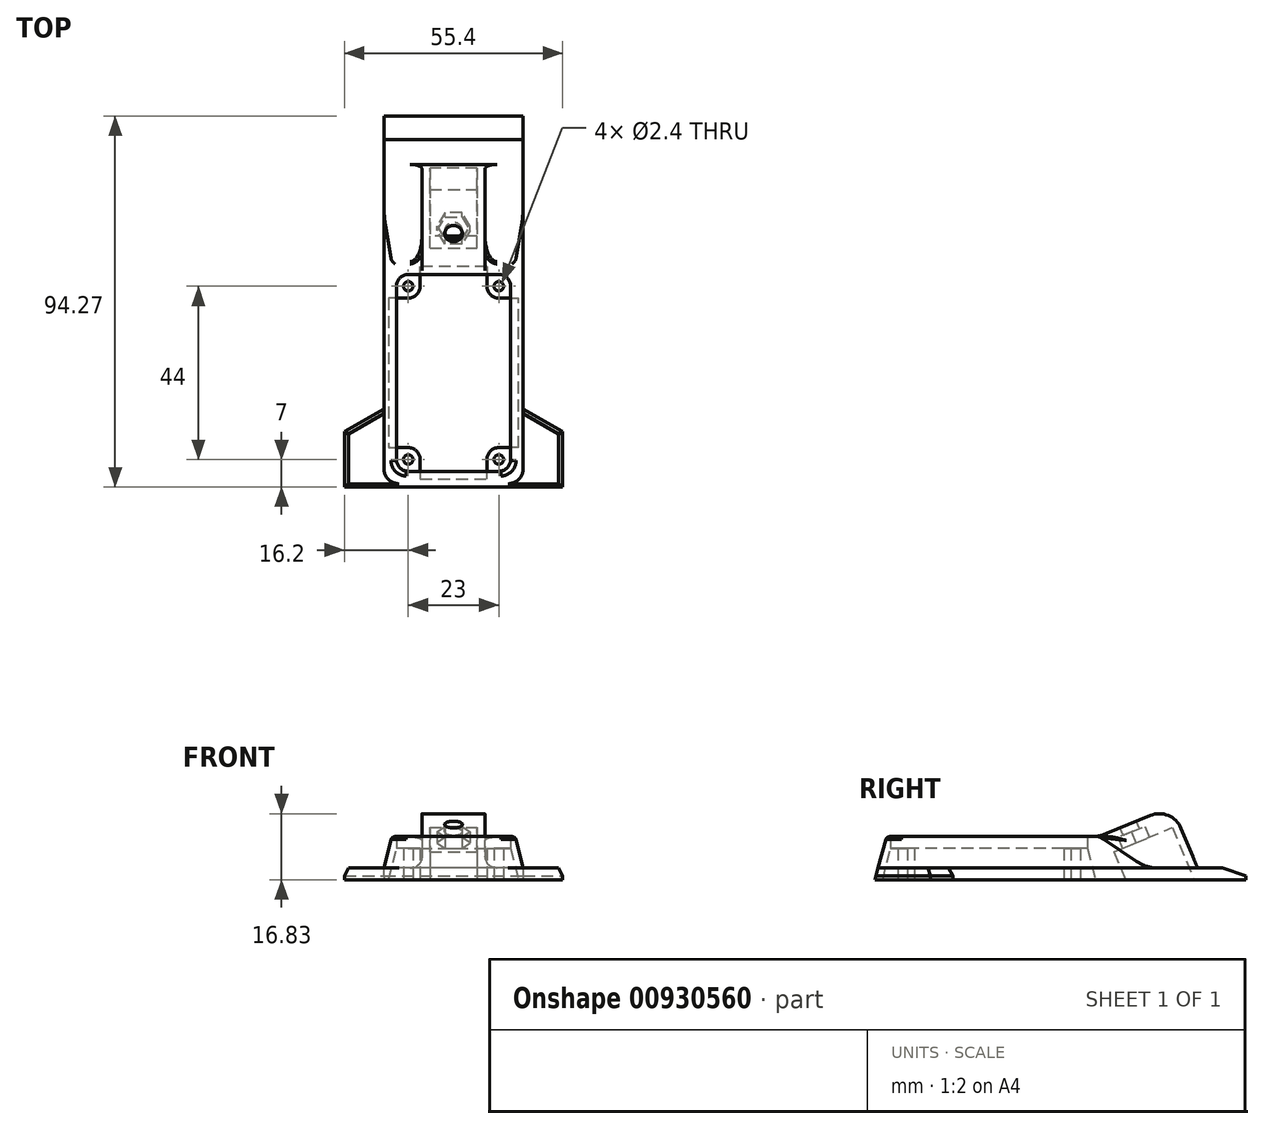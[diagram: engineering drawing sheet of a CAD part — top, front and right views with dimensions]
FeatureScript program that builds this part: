
annotation { "Feature Type Name" : "Feature", "Feature Type Description" : "" }
export const myFeature = defineFeature(function(context is Context, id is Id, definition is map)
    precondition{}
    {
        {
            var Q0;
            Q0=qCreatedBy(makeId("Top.planeOp"),FACE);
            var sketch = newSketch(context, id + "F0", { "sketchPlane" : qUnion([Q0])});
            skLineSegment(sketch, "E0", {"start": v(-28, 0) * mm, "end": v(28, 0) * mm, "construction": true});
            skLineSegment(sketch, "E1", {"start": v(28, 0) * mm, "end": v(28, 14.23) * mm, "construction": true});
            skLineSegment(sketch, "E2", {"start": v(28, 14.23) * mm, "end": v(18, 20) * mm, "construction": true});
            skLineSegment(sketch, "E3", {"start": v(18, 20) * mm, "end": v(18, 100.26) * mm, "construction": true});
            skLineSegment(sketch, "E4", {"start": v(18, 100.26) * mm, "end": v(-18, 100.26) * mm, "construction": true});
            skLineSegment(sketch, "E5", {"start": v(-18, 100.26) * mm, "end": v(-18, 20) * mm, "construction": true});
            skLineSegment(sketch, "E6", {"start": v(-18, 20) * mm, "end": v(-28, 14.23) * mm, "construction": true});
            skLineSegment(sketch, "E7", {"start": v(-28, 14.23) * mm, "end": v(-28, 0) * mm, "construction": true});
            skLineSegment(sketch, "E8", {"start": v(-18, 94.27) * mm, "end": v(18, 94.27) * mm, "construction": true});
            skLineSegment(sketch, "E9.bottom", {"start": v(-10.5, 55) * mm, "end": v(10.5, 55) * mm, "construction": true});
            skLineSegment(sketch, "E9.top", {"start": v(-10.5, 3) * mm, "end": v(10.5, 3) * mm, "construction": true});
            skLineSegment(sketch, "E9.left", {"start": v(-15.5, 50) * mm, "end": v(-15.5, 8) * mm, "construction": true});
            skLineSegment(sketch, "E9.right", {"start": v(15.5, 50) * mm, "end": v(15.5, 8) * mm, "construction": true});
            skLineSegment(sketch, "E10", {"start": v(-17.7, 19.83) * mm, "end": v(-17.7, 94.27) * mm});
            skLineSegment(sketch, "E11", {"start": v(-17.7, 94.27) * mm, "end": v(17.7, 94.27) * mm});
            skLineSegment(sketch, "E12", {"start": v(17.7, 94.27) * mm, "end": v(17.7, 19.83) * mm});
            skLineSegment(sketch, "E13", {"start": v(-17.7, 19.83) * mm, "end": v(-27.7, 14.05) * mm});
            skLineSegment(sketch, "E14", {"start": v(-27.7, 14.05) * mm, "end": v(-27.7, 0) * mm});
            skLineSegment(sketch, "E15", {"start": v(-27.7, 0) * mm, "end": v(27.7, 0) * mm});
            skLineSegment(sketch, "E16", {"start": v(27.7, 0) * mm, "end": v(27.7, 14.05) * mm});
            skLineSegment(sketch, "E17", {"start": v(27.7, 14.05) * mm, "end": v(17.7, 19.83) * mm});
            skCircle(sketch, "E18", {"center": v(-11.5, 51) * mm, "radius": 1.2 * mm});
            skCircle(sketch, "E19", {"center": v(11.5, 51) * mm, "radius": 1.2 * mm});
            skCircle(sketch, "E20", {"center": v(-11.5, 7) * mm, "radius": 1.2 * mm});
            skCircle(sketch, "E21", {"center": v(11.5, 7) * mm, "radius": 1.2 * mm});
            skArc(sketch, "E22", {"start": v(-11.5, 48) * mm, "mid": v(-9.38, 48.88) * mm, "end": v(-8.5, 51) * mm});
            skArc(sketch, "E23", {"start": v(8.5, 51) * mm, "mid": v(9.38, 48.88) * mm, "end": v(11.5, 48) * mm});
            skArc(sketch, "E24", {"start": v(-8.5, 7) * mm, "mid": v(-9.38, 9.12) * mm, "end": v(-11.5, 10) * mm});
            skArc(sketch, "E25", {"start": v(11.5, 10) * mm, "mid": v(9.38, 9.12) * mm, "end": v(8.5, 7) * mm});
            skLineSegment(sketch, "E26", {"start": v(-11.5, 48) * mm, "end": v(-14.5, 48) * mm});
            skLineSegment(sketch, "E27", {"start": v(-14.5, 48) * mm, "end": v(-14.5, 10) * mm});
            skLineSegment(sketch, "E28", {"start": v(-8.5, 54) * mm, "end": v(8.5, 54) * mm});
            skLineSegment(sketch, "E29", {"start": v(-8.5, 54) * mm, "end": v(-8.5, 51) * mm});
            skPoint(sketch, "E30.visualSharp", {"position": v(-15.5, 55) * mm});
            skArc(sketch, "E30.filletArc", {"start": v(-10.5, 55) * mm, "mid": v(-14.04, 53.54) * mm, "end": v(-15.5, 50) * mm, "construction": true});
            skPoint(sketch, "E31.visualSharp", {"position": v(15.5, 55) * mm});
            skArc(sketch, "E31.filletArc", {"start": v(15.5, 50) * mm, "mid": v(14.04, 53.54) * mm, "end": v(10.5, 55) * mm, "construction": true});
            skPoint(sketch, "E32.visualSharp", {"position": v(-15.5, 3) * mm});
            skArc(sketch, "E32.filletArc", {"start": v(-15.5, 8) * mm, "mid": v(-14.04, 4.46) * mm, "end": v(-10.5, 3) * mm, "construction": true});
            skPoint(sketch, "E33.visualSharp", {"position": v(15.5, 3) * mm});
            skArc(sketch, "E33.filletArc", {"start": v(10.5, 3) * mm, "mid": v(14.04, 4.46) * mm, "end": v(15.5, 8) * mm, "construction": true});
            skLineSegment(sketch, "E34", {"start": v(8.5, 54) * mm, "end": v(8.5, 51) * mm});
            skLineSegment(sketch, "E35", {"start": v(11.5, 48) * mm, "end": v(14.5, 48) * mm});
            skLineSegment(sketch, "E36", {"start": v(14.5, 48) * mm, "end": v(14.5, 10) * mm});
            skLineSegment(sketch, "E37", {"start": v(14.5, 10) * mm, "end": v(11.5, 10) * mm});
            skLineSegment(sketch, "E38", {"start": v(-11.5, 10) * mm, "end": v(-14.5, 10) * mm});
            skLineSegment(sketch, "E39", {"start": v(-8.5, 7) * mm, "end": v(-8.5, 4) * mm});
            skLineSegment(sketch, "E40", {"start": v(-8.5, 4) * mm, "end": v(8.5, 4) * mm});
            skLineSegment(sketch, "E41", {"start": v(8.5, 4) * mm, "end": v(8.5, 7) * mm});
            skSolve(sketch);
        }
        {
            var Q0;
            Q0=qSketchRegion(id+"F0",true);
            extrude(context, id + "F1", {"entities" : qUnion([Q0]), "depth" : 3 * mm, "offsetDistance" : 25 * mm});
        }
        {
            var Q0;
            Q0=makeQuery(id+"F1.opExtrude","SWEPT_FACE",FACE,{"disambiguationData":[OSD([sQuery(id+"F0.wireOp",EDGE,"E14")])]});
            var sketch = newSketch(context, id + "F2", { "sketchPlane" : qUnion([Q0])});
            skLineSegment(sketch, "E42", {"start": v(0, 0) * mm, "end": v(0, 3) * mm});
            skLineSegment(sketch, "E43", {"start": v(0, 3) * mm, "end": v(1.25, 3) * mm});
            skLineSegment(sketch, "E44", {"start": v(1.25, 3) * mm, "end": v(0, 0) * mm});
            skSolve(sketch);
        }
        {
            var Q0;
            Q0=qSketchRegion(id+"F2",true);
            var Q1;
            Q1=makeQuery(id+"F1.opExtrude","SWEPT_FACE",FACE,{"disambiguationData":[OSD([sQuery(id+"F0.wireOp",EDGE,"E16")])]});
            extrude(context, id + "F3", {"entities" : qUnion([Q0]), "operationType" : NewBodyOperationType.ADD, "endBound" : BoundingType.UP_TO_SURFACE, "oppositeDirection" : true, "depth" : 25 * mm, "endBoundEntityFace" : qUnion([Q1]), "offsetDistance" : 25 * mm});
        }
        {
            var Q0;
            Q0=makeQuery(id+"F3.boolean.opBoolean","MERGE",FACE,{"derivedFrom":[makeQuery(id+"F1.opExtrude","CAP_FACE",FACE,{"disambiguationData":[OSD([sQuery(id+"F0.wireOp",EDGE,"E10"),sQuery(id+"F0.wireOp",EDGE,"E11"),sQuery(id+"F0.wireOp",EDGE,"E12"),sQuery(id+"F0.wireOp",EDGE,"E13"),sQuery(id+"F0.wireOp",EDGE,"E14"),sQuery(id+"F0.wireOp",EDGE,"E15"),sQuery(id+"F0.wireOp",EDGE,"E16"),sQuery(id+"F0.wireOp",EDGE,"E17"),sQuery(id+"F0.wireOp",EDGE,"E18"),sQuery(id+"F0.wireOp",EDGE,"E19"),sQuery(id+"F0.wireOp",EDGE,"E20"),sQuery(id+"F0.wireOp",EDGE,"E21"),sQuery(id+"F0.wireOp",EDGE,"E22"),sQuery(id+"F0.wireOp",EDGE,"E23"),sQuery(id+"F0.wireOp",EDGE,"E24"),sQuery(id+"F0.wireOp",EDGE,"E25"),sQuery(id+"F0.wireOp",EDGE,"E26"),sQuery(id+"F0.wireOp",EDGE,"E27"),sQuery(id+"F0.wireOp",EDGE,"E28"),sQuery(id+"F0.wireOp",EDGE,"E29"),sQuery(id+"F0.wireOp",EDGE,"E34"),sQuery(id+"F0.wireOp",EDGE,"E35"),sQuery(id+"F0.wireOp",EDGE,"E36"),sQuery(id+"F0.wireOp",EDGE,"E37"),sQuery(id+"F0.wireOp",EDGE,"E38"),sQuery(id+"F0.wireOp",EDGE,"E39"),sQuery(id+"F0.wireOp",EDGE,"E40"),sQuery(id+"F0.wireOp",EDGE,"E41")])],"isStart":false}),makeQuery(id+"F3.opExtrude","SWEPT_FACE",FACE,{"disambiguationData":[OSD([sQuery(id+"F2.wireOp",EDGE,"E43")])]})]});
            var sketch = newSketch(context, id + "F4", { "sketchPlane" : qUnion([Q0])});
            skLineSegment(sketch, "E45", {"start": v(-17.7, 57) * mm, "end": v(-17.7, -1.25) * mm});
            skLineSegment(sketch, "E46", {"start": v(-17.7, -1.25) * mm, "end": v(17.7, -1.25) * mm});
            skLineSegment(sketch, "E47", {"start": v(17.7, -1.25) * mm, "end": v(17.7, 57) * mm});
            skLineSegment(sketch, "E48", {"start": v(-17.7, 57) * mm, "end": v(17.7, 57) * mm});
            skLineSegment(sketch, "E49.bottom", {"start": v(-11.5, 54) * mm, "end": v(11.5, 54) * mm});
            skLineSegment(sketch, "E49.top", {"start": v(-11.5, 4) * mm, "end": v(11.5, 4) * mm});
            skLineSegment(sketch, "E49.left", {"start": v(-14.5, 51) * mm, "end": v(-14.5, 7) * mm});
            skLineSegment(sketch, "E49.right", {"start": v(14.5, 51) * mm, "end": v(14.5, 7) * mm});
            skArc(sketch, "E50", {"start": v(-11.5, 54) * mm, "mid": v(-13.62, 53.12) * mm, "end": v(-14.5, 51) * mm});
            skArc(sketch, "E51", {"start": v(14.5, 51) * mm, "mid": v(13.62, 53.12) * mm, "end": v(11.5, 54) * mm});
            skArc(sketch, "E52", {"start": v(-14.5, 7) * mm, "mid": v(-13.62, 4.88) * mm, "end": v(-11.5, 4) * mm});
            skArc(sketch, "E53", {"start": v(11.5, 4) * mm, "mid": v(13.62, 4.88) * mm, "end": v(14.5, 7) * mm});
            skSolve(sketch);
        }
        {
            var Q0;
            Q0=qSketchRegion(id+"F4",true);
            extrude(context, id + "F5", {"entities" : qUnion([Q0]), "operationType" : NewBodyOperationType.ADD, "depth" : 8 * mm, "offsetDistance" : 25 * mm});
        }
        {
            var Q0;
            {var subQ0=sQuery(id+"F0.wireOp",EDGE,"E26");var subQ1=sQuery(id+"F0.wireOp",EDGE,"E27");var subQ2=sQuery(id+"F0.wireOp",EDGE,"E22");var subQ3=sQuery(id+"F0.wireOp",EDGE,"E18");var subQ4=sQuery(id+"F0.wireOp",EDGE,"E29");var subQ5=sQuery(id+"F0.wireOp",EDGE,"E28");Q0=makeQuery(id+"F5.boolean.opBoolean","SPLIT",FACE,{"disambiguationData":[TD([makeQuery(id+"F1.opExtrude","SWEPT_FACE",FACE,{"disambiguationData":[OSD([subQ3])]})])],"derivedFrom":makeQuery(id+"F3.boolean.opBoolean","MERGE",FACE,{"derivedFrom":[makeQuery(id+"F1.opExtrude","CAP_FACE",FACE,{"disambiguationData":[OSD([sQuery(id+"F0.wireOp",EDGE,"E10"),sQuery(id+"F0.wireOp",EDGE,"E11"),sQuery(id+"F0.wireOp",EDGE,"E12"),sQuery(id+"F0.wireOp",EDGE,"E13"),sQuery(id+"F0.wireOp",EDGE,"E14"),sQuery(id+"F0.wireOp",EDGE,"E15"),sQuery(id+"F0.wireOp",EDGE,"E16"),sQuery(id+"F0.wireOp",EDGE,"E17"),subQ3,sQuery(id+"F0.wireOp",EDGE,"E19"),sQuery(id+"F0.wireOp",EDGE,"E20"),sQuery(id+"F0.wireOp",EDGE,"E21"),subQ2,sQuery(id+"F0.wireOp",EDGE,"E23"),sQuery(id+"F0.wireOp",EDGE,"E24"),sQuery(id+"F0.wireOp",EDGE,"E25"),subQ0,subQ1,subQ5,subQ4,sQuery(id+"F0.wireOp",EDGE,"E34"),sQuery(id+"F0.wireOp",EDGE,"E35"),sQuery(id+"F0.wireOp",EDGE,"E36"),sQuery(id+"F0.wireOp",EDGE,"E37"),sQuery(id+"F0.wireOp",EDGE,"E38"),sQuery(id+"F0.wireOp",EDGE,"E39"),sQuery(id+"F0.wireOp",EDGE,"E40"),sQuery(id+"F0.wireOp",EDGE,"E41")])],"isStart":false}),makeQuery(id+"F3.opExtrude","SWEPT_FACE",FACE,{"disambiguationData":[OSD([sQuery(id+"F2.wireOp",EDGE,"E43")])]})]})});}
            var sketch = newSketch(context, id + "F6", { "sketchPlane" : qUnion([Q0])});
            skCircle(sketch, "E54", {"center": v(-11.5, 51) * mm, "radius": 1.2 * mm});
            skCircle(sketch, "E55", {"center": v(11.5, 51) * mm, "radius": 1.2 * mm});
            skCircle(sketch, "E56", {"center": v(-11.5, 7) * mm, "radius": 1.2 * mm});
            skCircle(sketch, "E57", {"center": v(11.5, 7) * mm, "radius": 1.2 * mm});
            skLineSegment(sketch, "E58", {"start": v(-14.5, 48) * mm, "end": v(-11.5, 48) * mm});
            skLineSegment(sketch, "E59", {"start": v(-14.5, 51) * mm, "end": v(-14.5, 48) * mm});
            skLineSegment(sketch, "E60", {"start": v(-11.5, 54) * mm, "end": v(-8.5, 54) * mm});
            skLineSegment(sketch, "E61", {"start": v(-8.5, 54) * mm, "end": v(-8.5, 51) * mm});
            skLineSegment(sketch, "E62", {"start": v(8.5, 51) * mm, "end": v(8.5, 54) * mm});
            skLineSegment(sketch, "E63", {"start": v(8.5, 54) * mm, "end": v(11.5, 54) * mm});
            skLineSegment(sketch, "E64", {"start": v(11.5, 48) * mm, "end": v(14.5, 48) * mm});
            skLineSegment(sketch, "E65", {"start": v(14.5, 48) * mm, "end": v(14.5, 51) * mm});
            skArc(sketch, "E66", {"start": v(-11.5, 54) * mm, "mid": v(-13.62, 53.12) * mm, "end": v(-14.5, 51) * mm});
            skArc(sketch, "E67", {"start": v(-11.5, 48) * mm, "mid": v(-9.38, 48.88) * mm, "end": v(-8.5, 51) * mm});
            skArc(sketch, "E68", {"start": v(8.5, 51) * mm, "mid": v(9.38, 48.88) * mm, "end": v(11.5, 48) * mm});
            skArc(sketch, "E69", {"start": v(14.5, 51) * mm, "mid": v(13.62, 53.12) * mm, "end": v(11.5, 54) * mm});
            skArc(sketch, "E70", {"start": v(-8.5, 7) * mm, "mid": v(-9.38, 9.12) * mm, "end": v(-11.5, 10) * mm});
            skArc(sketch, "E71", {"start": v(-14.5, 7) * mm, "mid": v(-13.62, 4.88) * mm, "end": v(-11.5, 4) * mm});
            skLineSegment(sketch, "E72", {"start": v(-11.5, 10) * mm, "end": v(-14.5, 10) * mm});
            skLineSegment(sketch, "E73", {"start": v(-14.5, 7) * mm, "end": v(-14.5, 10) * mm});
            skLineSegment(sketch, "E74", {"start": v(-11.5, 4) * mm, "end": v(-8.5, 4) * mm});
            skLineSegment(sketch, "E75", {"start": v(-8.5, 4) * mm, "end": v(-8.5, 7) * mm});
            skArc(sketch, "E76", {"start": v(11.5, 10) * mm, "mid": v(9.38, 9.12) * mm, "end": v(8.5, 7) * mm});
            skArc(sketch, "E77", {"start": v(11.5, 4) * mm, "mid": v(13.62, 4.88) * mm, "end": v(14.5, 7) * mm});
            skLineSegment(sketch, "E78", {"start": v(8.5, 7) * mm, "end": v(8.5, 4) * mm});
            skLineSegment(sketch, "E79", {"start": v(8.5, 4) * mm, "end": v(11.5, 4) * mm});
            skLineSegment(sketch, "E80", {"start": v(11.5, 10) * mm, "end": v(14.5, 10) * mm});
            skLineSegment(sketch, "E81", {"start": v(14.5, 10) * mm, "end": v(14.5, 7) * mm});
            skSolve(sketch);
        }
        {
            var Q0;
            Q0=qSketchRegion(id+"F6",true);
            extrude(context, id + "F7", {"entities" : qUnion([Q0]), "operationType" : NewBodyOperationType.ADD, "depth" : 5 * mm, "offsetDistance" : 25 * mm});
        }
        {
            var Q0;
            Q0=qCreatedBy(makeId("Right.planeOp"),FACE);
            var sketch = newSketch(context, id + "F8", { "sketchPlane" : qUnion([Q0])});
            skLineSegment(sketch, "E82", {"start": v(81.98, 3) * mm, "end": v(57, 3) * mm});
            skLineSegment(sketch, "E83", {"start": v(57, 3) * mm, "end": v(57, 11) * mm});
            skLineSegment(sketch, "E84", {"start": v(57, 11) * mm, "end": v(75.47, 18.67) * mm});
            skLineSegment(sketch, "E85", {"start": v(75.47, 18.67) * mm, "end": v(81.98, 3) * mm});
            skSolve(sketch);
        }
        {
            var Q0;
            Q0=qSketchRegion(id+"F8",true);
            extrude(context, id + "F9", {"entities" : qUnion([Q0]), "operationType" : NewBodyOperationType.ADD, "depth" : 8 * mm, "offsetDistance" : 25 * mm});
        }
        {
            var Q0;
            Q0=qSketchRegion(id+"F8",true);
            extrude(context, id + "F10", {"entities" : qUnion([Q0]), "operationType" : NewBodyOperationType.ADD, "oppositeDirection" : true, "depth" : 8 * mm, "offsetDistance" : 25 * mm});
        }
        {
            var Q0;
            Q0=makeQuery(id+"F3.boolean.opBoolean","MERGE",FACE,{"derivedFrom":[makeQuery(id+"F1.opExtrude","SWEPT_FACE",FACE,{"disambiguationData":[OSD([sQuery(id+"F0.wireOp",EDGE,"E14")])]}),makeQuery(id+"F3.opExtrude","CAP_FACE",FACE,{"disambiguationData":[OSD([sQuery(id+"F2.wireOp",EDGE,"E42"),sQuery(id+"F2.wireOp",EDGE,"E43"),sQuery(id+"F2.wireOp",EDGE,"E44")])],"isStart":true})]});
            var sketch = newSketch(context, id + "F11", { "sketchPlane" : qUnion([Q0])});
            skLineSegment(sketch, "E86", {"start": v(0, 0) * mm, "end": v(-3, 11) * mm});
            skLineSegment(sketch, "E87", {"start": v(-3, 11) * mm, "end": v(1.25, 11) * mm});
            skLineSegment(sketch, "E88", {"start": v(1.25, 11) * mm, "end": v(1.25, 3) * mm});
            skLineSegment(sketch, "E89", {"start": v(1.25, 3) * mm, "end": v(0, 0) * mm});
            skSolve(sketch);
        }
        {
            var Q0;
            Q0=qSketchRegion(id+"F11",true);
            var Q1;
            Q1=makeQuery(id+"F3.boolean.opBoolean","MERGE",FACE,{"derivedFrom":[makeQuery(id+"F1.opExtrude","SWEPT_FACE",FACE,{"disambiguationData":[OSD([sQuery(id+"F0.wireOp",EDGE,"E16")])]}),makeQuery(id+"F3.opExtrude","CAP_FACE",FACE,{"disambiguationData":[OSD([sQuery(id+"F2.wireOp",EDGE,"E42"),sQuery(id+"F2.wireOp",EDGE,"E43"),sQuery(id+"F2.wireOp",EDGE,"E44")])],"isStart":false})]});
            extrude(context, id + "F12", {"entities" : qUnion([Q0]), "operationType" : NewBodyOperationType.REMOVE, "endBound" : BoundingType.UP_TO_SURFACE, "oppositeDirection" : true, "depth" : 25 * mm, "endBoundEntityFace" : qUnion([Q1]), "offsetDistance" : 25 * mm});
        }
        {
            var Q0;
            {var subQ0=sQuery(id+"F8.wireOp",EDGE,"E84");Q0=makeQuery(id+"F10.boolean.opBoolean","MERGE",FACE,{"derivedFrom":[makeQuery(id+"F9.opExtrude","SWEPT_FACE",FACE,{"disambiguationData":[OSD([subQ0])]}),makeQuery(id+"F10.opExtrude","SWEPT_FACE",FACE,{"disambiguationData":[OSD([subQ0])]})]});}
            var sketch = newSketch(context, id + "F13", { "sketchPlane" : qUnion([Q0])});
            skCircle(sketch, "E90", {"center": v(0, 64.86) * mm, "radius": 2.25 * mm});
            skSolve(sketch);
        }
        {
            var Q0;
            Q0=qSketchRegion(id+"F13",true);
            extrude(context, id + "F14", {"entities" : qUnion([Q0]), "operationType" : NewBodyOperationType.REMOVE, "endBound" : BoundingType.UP_TO_NEXT, "oppositeDirection" : true, "depth" : 25 * mm, "offsetDistance" : 25 * mm});
        }
        {
            var Q0;
            {var subQ0=sQuery(id+"F8.wireOp",EDGE,"E84");Q0=makeQuery(id+"F10.boolean.opBoolean","MERGE",FACE,{"derivedFrom":[makeQuery(id+"F9.opExtrude","SWEPT_FACE",FACE,{"disambiguationData":[OSD([subQ0])]}),makeQuery(id+"F10.opExtrude","SWEPT_FACE",FACE,{"disambiguationData":[OSD([subQ0])]})]});}
            cPlane(context, id + "F15", {"entities" : qUnion([Q0]), "cplaneType" : CPlaneType.OFFSET, "offset" : 25 * mm, "oppositeDirection" : true, "width" : 150 * mm, "height" : 150 * mm});
        }
        {
            var Q0;
            Q0=qCreatedBy(id+"F15.planeOp",FACE);
            var sketch = newSketch(context, id + "F16", { "sketchPlane" : qUnion([Q0])});
            skLineSegment(sketch, "E91.bottom", {"start": v(-6, 58.86) * mm, "end": v(6, 58.86) * mm});
            skLineSegment(sketch, "E91.top", {"start": v(-6, 74.86) * mm, "end": v(6, 74.86) * mm});
            skLineSegment(sketch, "E91.left", {"start": v(-6, 58.86) * mm, "end": v(-6, 74.86) * mm});
            skLineSegment(sketch, "E91.right", {"start": v(6, 58.86) * mm, "end": v(6, 74.86) * mm});
            skSolve(sketch);
        }
        {
            var Q0;
            Q0=qSketchRegion(id+"F16",true);
            extrude(context, id + "F17", {"entities" : qUnion([Q0]), "operationType" : NewBodyOperationType.REMOVE, "depth" : 20 * mm, "offsetDistance" : 25 * mm});
        }
        {
            var Q0;
            Q0=qCreatedBy(id+"F15.planeOp",FACE);
            var sketch = newSketch(context, id + "F18", { "sketchPlane" : qUnion([Q0])});
            skCircle(sketch, "E92.cCircle", {"center": v(0, 64.86) * mm, "radius": 4.25 * mm, "construction": true});
            skLineSegment(sketch, "E92.0", {"start": v(4.25, 64.86) * mm, "end": v(2.13, 61.18) * mm});
            skLineSegment(sketch, "E92.1", {"start": v(2.13, 61.18) * mm, "end": v(-2.13, 61.18) * mm});
            skLineSegment(sketch, "E92.2", {"start": v(-2.12, 61.18) * mm, "end": v(-4.25, 64.86) * mm});
            skLineSegment(sketch, "E92.3", {"start": v(-4.25, 64.86) * mm, "end": v(-2.12, 68.54) * mm});
            skLineSegment(sketch, "E92.4", {"start": v(-2.12, 68.54) * mm, "end": v(2.13, 68.54) * mm});
            skLineSegment(sketch, "E92.5", {"start": v(2.13, 68.54) * mm, "end": v(4.25, 64.86) * mm});
            skSolve(sketch);
        }
        {
            var Q0;
            Q0=qSketchRegion(id+"F18",true);
            extrude(context, id + "F19", {"entities" : qUnion([Q0]), "operationType" : NewBodyOperationType.REMOVE, "depth" : 23 * mm, "offsetDistance" : 25 * mm});
        }
        {
            var Q0;
            Q0=makeQuery(id+"F5.opExtrude","CAP_EDGE",EDGE,{"disambiguationData":[OSD([sQuery(id+"F4.wireOp",EDGE,"E47")])],"isStart":false});
            var Q1;
            Q1=makeQuery(id+"F5.opExtrude","CAP_EDGE",EDGE,{"disambiguationData":[OSD([sQuery(id+"F4.wireOp",EDGE,"E45")])],"isStart":false});
            chamfer(context, id + "F20", {"entities" : qUnion([Q0, Q1]), "chamferType" : ChamferType.TWO_OFFSETS, "width1" : 2 * mm, "oppositeDirection" : false, "width2" : 8 * mm, "tangentPropagation" : true});
        }
        {
            var Q0;
            Q0=makeQuery(id+"F3.boolean.opBoolean","MERGE",EDGE,{"derivedFrom":[makeQuery(id+"F1.opExtrude","CAP_EDGE",EDGE,{"disambiguationData":[OSD([sQuery(id+"F0.wireOp",EDGE,"E16")])],"isStart":false}),makeQuery(id+"F3.opExtrude","CAP_EDGE",EDGE,{"disambiguationData":[OSD([sQuery(id+"F2.wireOp",EDGE,"E43")])],"isStart":false})]});
            var Q1;
            Q1=makeQuery(id+"F1.opExtrude","CAP_EDGE",EDGE,{"disambiguationData":[OSD([sQuery(id+"F0.wireOp",EDGE,"E17")])],"isStart":false});
            var Q2;
            Q2=makeQuery(id+"F3.boolean.opBoolean","MERGE",EDGE,{"derivedFrom":[makeQuery(id+"F1.opExtrude","CAP_EDGE",EDGE,{"disambiguationData":[OSD([sQuery(id+"F0.wireOp",EDGE,"E14")])],"isStart":false}),makeQuery(id+"F3.opExtrude","CAP_EDGE",EDGE,{"disambiguationData":[OSD([sQuery(id+"F2.wireOp",EDGE,"E43")])],"isStart":true})]});
            var Q3;
            Q3=makeQuery(id+"F1.opExtrude","CAP_EDGE",EDGE,{"disambiguationData":[OSD([sQuery(id+"F0.wireOp",EDGE,"E13")])],"isStart":false});
            chamfer(context, id + "F21", {"entities" : qUnion([Q0, Q1, Q2, Q3]), "chamferType" : ChamferType.TWO_OFFSETS, "width1" : 1 * mm, "oppositeDirection" : false, "width2" : 2 * mm, "tangentPropagation" : true});
        }
        {
            var Q0;
            {var subQ0=sQuery(id+"F0.wireOp",EDGE,"E12");var subQ1=sQuery(id+"F4.wireOp",EDGE,"E48");Q0=makeQuery(id+"F9.boolean.opBoolean","SPLIT",EDGE,{"disambiguationData":[TD([makeQuery(id+"F1.opExtrude","SWEPT_FACE",FACE,{"disambiguationData":[OSD([subQ0])]})])],"derivedFrom":makeQuery(id+"F5.opExtrude","CAP_EDGE",EDGE,{"disambiguationData":[OSD([subQ1])],"isStart":true})});}
            var Q1;
            {var subQ0=sQuery(id+"F0.wireOp",EDGE,"E10");var subQ1=sQuery(id+"F4.wireOp",EDGE,"E48");Q1=makeQuery(id+"F9.boolean.opBoolean","SPLIT",EDGE,{"disambiguationData":[TD([makeQuery(id+"F1.opExtrude","SWEPT_FACE",FACE,{"disambiguationData":[OSD([subQ0])]})])],"derivedFrom":makeQuery(id+"F5.opExtrude","CAP_EDGE",EDGE,{"disambiguationData":[OSD([subQ1])],"isStart":true})});}
            chamfer(context, id + "F22", {"entities" : qUnion([Q0, Q1]), "chamferType" : ChamferType.TWO_OFFSETS, "width1" : 12 * mm, "oppositeDirection" : false, "width2" : 8 * mm, "tangentPropagation" : true});
        }
        {
            var Q0;
            {var subQ0=sQuery(id+"F8.wireOp",EDGE,"E84");var subQ1=sQuery(id+"F8.wireOp",EDGE,"E83");var subQ2=sQuery(id+"F4.wireOp",EDGE,"E48");var subQ4=makeQuery(id+"F5.opExtrude","CAP_EDGE",EDGE,{"disambiguationData":[OSD([subQ2])],"isStart":false});Q0=makeQuery(id+"F10.boolean.opBoolean","MERGE",EDGE,{"derivedFrom":[makeQuery(id+"F9.boolean.opBoolean","MERGE",EDGE,{"derivedFrom":[subQ4,makeQuery(id+"F9.opExtrude","SWEPT_EDGE",EDGE,{"disambiguationData":[OSD([subQ1,subQ0])]})]}),makeQuery(id+"F9.boolean.opBoolean","SPLIT",EDGE,{"disambiguationData":[TD([makeQuery(id+"F1.opExtrude","SWEPT_FACE",FACE,{"disambiguationData":[OSD([sQuery(id+"F0.wireOp",EDGE,"E10")])]})])],"derivedFrom":subQ4}),makeQuery(id+"F10.opExtrude","SWEPT_EDGE",EDGE,{"disambiguationData":[OSD([subQ1,subQ0])]})]});}
            var Q1;
            {var subQ0=sQuery(id+"F0.wireOp",EDGE,"E12");var subQ1=makeQuery(id+"F1.opExtrude","SWEPT_FACE",FACE,{"disambiguationData":[OSD([subQ0])]});var subQ2=sQuery(id+"F0.wireOp",EDGE,"E11");var subQ3=sQuery(id+"F0.wireOp",EDGE,"E10");var subQ4=sQuery(id+"F4.wireOp",EDGE,"E48");var subQ7=makeQuery(id+"F3.opExtrude","SWEPT_FACE",FACE,{"disambiguationData":[OSD([sQuery(id+"F2.wireOp",EDGE,"E43")])]});var subQ8=makeQuery(id+"F1.opExtrude","CAP_FACE",FACE,{"disambiguationData":[OSD([subQ3,subQ2,subQ0,sQuery(id+"F0.wireOp",EDGE,"E13"),sQuery(id+"F0.wireOp",EDGE,"E14"),sQuery(id+"F0.wireOp",EDGE,"E15"),sQuery(id+"F0.wireOp",EDGE,"E16"),sQuery(id+"F0.wireOp",EDGE,"E17"),sQuery(id+"F0.wireOp",EDGE,"E18"),sQuery(id+"F0.wireOp",EDGE,"E19"),sQuery(id+"F0.wireOp",EDGE,"E20"),sQuery(id+"F0.wireOp",EDGE,"E21"),sQuery(id+"F0.wireOp",EDGE,"E22"),sQuery(id+"F0.wireOp",EDGE,"E23"),sQuery(id+"F0.wireOp",EDGE,"E24"),sQuery(id+"F0.wireOp",EDGE,"E25"),sQuery(id+"F0.wireOp",EDGE,"E26"),sQuery(id+"F0.wireOp",EDGE,"E27"),sQuery(id+"F0.wireOp",EDGE,"E28"),sQuery(id+"F0.wireOp",EDGE,"E29"),sQuery(id+"F0.wireOp",EDGE,"E34"),sQuery(id+"F0.wireOp",EDGE,"E35"),sQuery(id+"F0.wireOp",EDGE,"E36"),sQuery(id+"F0.wireOp",EDGE,"E37"),sQuery(id+"F0.wireOp",EDGE,"E38"),sQuery(id+"F0.wireOp",EDGE,"E39"),sQuery(id+"F0.wireOp",EDGE,"E40"),sQuery(id+"F0.wireOp",EDGE,"E41")])],"isStart":false});Q1=makeQuery(id+"F22.opChamfer","BLEND_EDGE",EDGE,{"blendedFrom":[makeQuery(id+"F9.boolean.opBoolean","SPLIT",EDGE,{"disambiguationData":[TD([subQ1])],"derivedFrom":makeQuery(id+"F5.opExtrude","CAP_EDGE",EDGE,{"disambiguationData":[OSD([subQ4])],"isStart":true})}),makeQuery(id+"F5.boolean.opBoolean","SPLIT",FACE,{"disambiguationData":[TD([makeQuery(id+"F1.opExtrude","SWEPT_FACE",FACE,{"disambiguationData":[OSD([subQ2])]})])],"derivedFrom":makeQuery(id+"F3.boolean.opBoolean","MERGE",FACE,{"derivedFrom":[subQ8,subQ7]})})],"blendedInto":[makeQuery(id+"F5.boolean.opBoolean","SPLIT",FACE,{"disambiguationData":[TD([makeQuery(id+"F1.opExtrude","SWEPT_FACE",FACE,{"disambiguationData":[OSD([subQ2])]})])],"derivedFrom":makeQuery(id+"F3.boolean.opBoolean","MERGE",FACE,{"derivedFrom":[subQ8,subQ7]})})]});}
            var Q2;
            {var subQ1=sQuery(id+"F0.wireOp",EDGE,"E12");var subQ2=sQuery(id+"F0.wireOp",EDGE,"E11");var subQ3=sQuery(id+"F0.wireOp",EDGE,"E10");var subQ4=makeQuery(id+"F1.opExtrude","SWEPT_FACE",FACE,{"disambiguationData":[OSD([subQ3])]});var subQ5=sQuery(id+"F4.wireOp",EDGE,"E48");var subQ7=makeQuery(id+"F3.opExtrude","SWEPT_FACE",FACE,{"disambiguationData":[OSD([sQuery(id+"F2.wireOp",EDGE,"E43")])]});var subQ8=makeQuery(id+"F1.opExtrude","CAP_FACE",FACE,{"disambiguationData":[OSD([subQ3,subQ2,subQ1,sQuery(id+"F0.wireOp",EDGE,"E13"),sQuery(id+"F0.wireOp",EDGE,"E14"),sQuery(id+"F0.wireOp",EDGE,"E15"),sQuery(id+"F0.wireOp",EDGE,"E16"),sQuery(id+"F0.wireOp",EDGE,"E17"),sQuery(id+"F0.wireOp",EDGE,"E18"),sQuery(id+"F0.wireOp",EDGE,"E19"),sQuery(id+"F0.wireOp",EDGE,"E20"),sQuery(id+"F0.wireOp",EDGE,"E21"),sQuery(id+"F0.wireOp",EDGE,"E22"),sQuery(id+"F0.wireOp",EDGE,"E23"),sQuery(id+"F0.wireOp",EDGE,"E24"),sQuery(id+"F0.wireOp",EDGE,"E25"),sQuery(id+"F0.wireOp",EDGE,"E26"),sQuery(id+"F0.wireOp",EDGE,"E27"),sQuery(id+"F0.wireOp",EDGE,"E28"),sQuery(id+"F0.wireOp",EDGE,"E29"),sQuery(id+"F0.wireOp",EDGE,"E34"),sQuery(id+"F0.wireOp",EDGE,"E35"),sQuery(id+"F0.wireOp",EDGE,"E36"),sQuery(id+"F0.wireOp",EDGE,"E37"),sQuery(id+"F0.wireOp",EDGE,"E38"),sQuery(id+"F0.wireOp",EDGE,"E39"),sQuery(id+"F0.wireOp",EDGE,"E40"),sQuery(id+"F0.wireOp",EDGE,"E41")])],"isStart":false});Q2=makeQuery(id+"F22.opChamfer","BLEND_EDGE",EDGE,{"blendedFrom":[makeQuery(id+"F9.boolean.opBoolean","SPLIT",EDGE,{"disambiguationData":[TD([subQ4])],"derivedFrom":makeQuery(id+"F5.opExtrude","CAP_EDGE",EDGE,{"disambiguationData":[OSD([subQ5])],"isStart":true})}),makeQuery(id+"F5.boolean.opBoolean","SPLIT",FACE,{"disambiguationData":[TD([makeQuery(id+"F1.opExtrude","SWEPT_FACE",FACE,{"disambiguationData":[OSD([subQ2])]})])],"derivedFrom":makeQuery(id+"F3.boolean.opBoolean","MERGE",FACE,{"derivedFrom":[subQ8,subQ7]})})],"blendedInto":[makeQuery(id+"F5.boolean.opBoolean","SPLIT",FACE,{"disambiguationData":[TD([makeQuery(id+"F1.opExtrude","SWEPT_FACE",FACE,{"disambiguationData":[OSD([subQ2])]})])],"derivedFrom":makeQuery(id+"F3.boolean.opBoolean","MERGE",FACE,{"derivedFrom":[subQ8,subQ7]})})]});}
            fillet(context, id + "F23", {"entities" : qUnion([Q0, Q1, Q2]), "radius" : 10 * mm, "tangentPropagation" : true, "allowEdgeOverflow" : false});
        }
        {
            var Q0;
            {var subQ0=sQuery(id+"F8.wireOp",EDGE,"E85");var subQ1=sQuery(id+"F8.wireOp",EDGE,"E84");Q0=makeQuery(id+"F10.boolean.opBoolean","MERGE",EDGE,{"derivedFrom":[makeQuery(id+"F9.opExtrude","SWEPT_EDGE",EDGE,{"disambiguationData":[OSD([subQ1,subQ0])]}),makeQuery(id+"F10.opExtrude","SWEPT_EDGE",EDGE,{"disambiguationData":[OSD([subQ1,subQ0])]})]});}
            fillet(context, id + "F24", {"entities" : qUnion([Q0]), "radius" : 6 * mm, "tangentPropagation" : true, "allowEdgeOverflow" : false});
        }
        {
            var Q0;
            {var subQ0=makeQuery(id+"F9.opExtrude","CAP_FACE",FACE,{"disambiguationData":[OSD([sQuery(id+"F8.wireOp",EDGE,"E82"),sQuery(id+"F8.wireOp",EDGE,"E83"),sQuery(id+"F8.wireOp",EDGE,"E84"),sQuery(id+"F8.wireOp",EDGE,"E85")])],"isStart":false});var subQ1=sQuery(id+"F0.wireOp",EDGE,"E12");var subQ2=sQuery(id+"F4.wireOp",EDGE,"E48");Q0=makeQuery(id+"F22.opChamfer","BLEND_EDGE",EDGE,{"blendedFrom":[makeQuery(id+"F9.boolean.opBoolean","SPLIT",EDGE,{"disambiguationData":[TD([makeQuery(id+"F1.opExtrude","SWEPT_FACE",FACE,{"disambiguationData":[OSD([subQ1])]})])],"derivedFrom":makeQuery(id+"F5.opExtrude","CAP_EDGE",EDGE,{"disambiguationData":[OSD([subQ2])],"isStart":true})}),subQ0],"blendedInto":[subQ0]});}
            var Q1;
            {var subQ0=sQuery(id+"F8.wireOp",EDGE,"E85");var subQ1=sQuery(id+"F8.wireOp",EDGE,"E82");Q1=makeQuery(id+"F10.boolean.opBoolean","MERGE",EDGE,{"derivedFrom":[makeQuery(id+"F9.opExtrude","SWEPT_EDGE",EDGE,{"disambiguationData":[OSD([subQ1,subQ0])]}),makeQuery(id+"F10.opExtrude","SWEPT_EDGE",EDGE,{"disambiguationData":[OSD([subQ1,subQ0])]})]});}
            var Q2;
            {var subQ0=sQuery(id+"F8.wireOp",EDGE,"E85");var subQ1=sQuery(id+"F8.wireOp",EDGE,"E84");var subQ2=sQuery(id+"F8.wireOp",EDGE,"E83");var subQ3=sQuery(id+"F8.wireOp",EDGE,"E82");var subQ4=sQuery(id+"F0.wireOp",EDGE,"E10");var subQ5=sQuery(id+"F4.wireOp",EDGE,"E48");Q2=makeQuery(id+"F22.opChamfer","BLEND_EDGE",EDGE,{"blendedFrom":[makeQuery(id+"F9.boolean.opBoolean","SPLIT",EDGE,{"disambiguationData":[TD([makeQuery(id+"F1.opExtrude","SWEPT_FACE",FACE,{"disambiguationData":[OSD([subQ4])]})])],"derivedFrom":makeQuery(id+"F5.opExtrude","CAP_EDGE",EDGE,{"disambiguationData":[OSD([subQ5])],"isStart":true})}),makeQuery(id+"F10.opExtrude","CAP_FACE",FACE,{"disambiguationData":[OSD([subQ3,subQ2,subQ1,subQ0])],"isStart":false})],"blendedInto":[makeQuery(id+"F10.opExtrude","CAP_FACE",FACE,{"disambiguationData":[OSD([subQ3,subQ2,subQ1,subQ0])],"isStart":false})]});}
            fillet(context, id + "F25", {"entities" : qUnion([Q0, Q1, Q2]), "radius" : 3 * mm, "tangentPropagation" : true, "allowEdgeOverflow" : false});
        }
        {
            var Q0;
            Q0=makeQuery(id+"F1.opExtrude","CAP_EDGE",EDGE,{"disambiguationData":[OSD([sQuery(id+"F0.wireOp",EDGE,"E11")])],"isStart":false});
            chamfer(context, id + "F26", {"entities" : qUnion([Q0]), "chamferType" : ChamferType.TWO_OFFSETS, "width1" : 2 * mm, "oppositeDirection" : false, "width2" : 6 * mm, "tangentPropagation" : true});
        }
        {
            var Q0;
            Q0=makeQuery(id+"F20.opChamfer","BLEND_EDGE",EDGE,{"blendedFrom":[makeQuery(id+"F5.opExtrude","CAP_EDGE",EDGE,{"disambiguationData":[OSD([sQuery(id+"F4.wireOp",EDGE,"E47")])],"isStart":false}),makeQuery(id+"F12.boolean.opBoolean","COPY",FACE,{"derivedFrom":makeQuery(id+"F12.opExtrude","SWEPT_FACE",FACE,{"disambiguationData":[OSD([sQuery(id+"F11.wireOp",EDGE,"E86")])]})})],"blendedInto":[makeQuery(id+"F12.boolean.opBoolean","COPY",FACE,{"derivedFrom":makeQuery(id+"F12.opExtrude","SWEPT_FACE",FACE,{"disambiguationData":[OSD([sQuery(id+"F11.wireOp",EDGE,"E86")])]})})]});
            var Q1;
            Q1=makeQuery(id+"F20.opChamfer","BLEND_EDGE",EDGE,{"blendedFrom":[makeQuery(id+"F5.opExtrude","CAP_EDGE",EDGE,{"disambiguationData":[OSD([sQuery(id+"F4.wireOp",EDGE,"E45")])],"isStart":false}),makeQuery(id+"F12.boolean.opBoolean","COPY",FACE,{"derivedFrom":makeQuery(id+"F12.opExtrude","SWEPT_FACE",FACE,{"disambiguationData":[OSD([sQuery(id+"F11.wireOp",EDGE,"E86")])]})})],"blendedInto":[makeQuery(id+"F12.boolean.opBoolean","COPY",FACE,{"derivedFrom":makeQuery(id+"F12.opExtrude","SWEPT_FACE",FACE,{"disambiguationData":[OSD([sQuery(id+"F11.wireOp",EDGE,"E86")])]})})]});
            fillet(context, id + "F27", {"entities" : qUnion([Q0, Q1]), "radius" : 4 * mm, "tangentPropagation" : true, "allowEdgeOverflow" : false});
        }
        {
            var Q0;
            Q0=makeQuery(id+"F1.opExtrude","CAP_EDGE",EDGE,{"disambiguationData":[OSD([sQuery(id+"F0.wireOp",EDGE,"E36")])],"isStart":true});
            var Q1;
            Q1=makeQuery(id+"F1.opExtrude","CAP_EDGE",EDGE,{"disambiguationData":[OSD([sQuery(id+"F0.wireOp",EDGE,"E28")])],"isStart":true});
            var Q2;
            Q2=makeQuery(id+"F1.opExtrude","CAP_EDGE",EDGE,{"disambiguationData":[OSD([sQuery(id+"F0.wireOp",EDGE,"E27")])],"isStart":true});
            var Q3;
            Q3=makeQuery(id+"F1.opExtrude","CAP_EDGE",EDGE,{"disambiguationData":[OSD([sQuery(id+"F0.wireOp",EDGE,"E40")])],"isStart":true});
            chamfer(context, id + "F28", {"entities" : qUnion([Q0, Q1, Q2, Q3]), "chamferType" : ChamferType.TWO_OFFSETS, "width1" : 8 * mm, "oppositeDirection" : false, "width2" : 2 * mm, "tangentPropagation" : true});
        }
        {
            var Q0;
            {var subQ0=sQuery(id+"F4.wireOp",EDGE,"E45");Q0=makeQuery(id+"F27.opFillet","BLEND_EDGE",EDGE,{"blendedFrom":[makeQuery(id+"F20.opChamfer","BLEND_EDGE",EDGE,{"blendedFrom":[makeQuery(id+"F5.opExtrude","CAP_EDGE",EDGE,{"disambiguationData":[OSD([subQ0])],"isStart":false}),makeQuery(id+"F12.boolean.opBoolean","COPY",FACE,{"derivedFrom":makeQuery(id+"F12.opExtrude","SWEPT_FACE",FACE,{"disambiguationData":[OSD([sQuery(id+"F11.wireOp",EDGE,"E86")])]})})],"blendedInto":[makeQuery(id+"F12.boolean.opBoolean","COPY",FACE,{"derivedFrom":makeQuery(id+"F12.opExtrude","SWEPT_FACE",FACE,{"disambiguationData":[OSD([sQuery(id+"F11.wireOp",EDGE,"E86")])]})})]}),makeQuery(id+"F5.opExtrude","CAP_FACE",FACE,{"disambiguationData":[OSD([subQ0,sQuery(id+"F4.wireOp",EDGE,"E46"),sQuery(id+"F4.wireOp",EDGE,"E47"),sQuery(id+"F4.wireOp",EDGE,"E48"),sQuery(id+"F4.wireOp",EDGE,"E49.bottom"),sQuery(id+"F4.wireOp",EDGE,"E49.top"),sQuery(id+"F4.wireOp",EDGE,"E49.left"),sQuery(id+"F4.wireOp",EDGE,"E49.right"),sQuery(id+"F4.wireOp",EDGE,"E50"),sQuery(id+"F4.wireOp",EDGE,"E51"),sQuery(id+"F4.wireOp",EDGE,"E52"),sQuery(id+"F4.wireOp",EDGE,"E53")])],"isStart":false})],"blendedInto":[makeQuery(id+"F5.opExtrude","CAP_FACE",FACE,{"disambiguationData":[OSD([subQ0,sQuery(id+"F4.wireOp",EDGE,"E46"),sQuery(id+"F4.wireOp",EDGE,"E47"),sQuery(id+"F4.wireOp",EDGE,"E48"),sQuery(id+"F4.wireOp",EDGE,"E49.bottom"),sQuery(id+"F4.wireOp",EDGE,"E49.top"),sQuery(id+"F4.wireOp",EDGE,"E49.left"),sQuery(id+"F4.wireOp",EDGE,"E49.right"),sQuery(id+"F4.wireOp",EDGE,"E50"),sQuery(id+"F4.wireOp",EDGE,"E51"),sQuery(id+"F4.wireOp",EDGE,"E52"),sQuery(id+"F4.wireOp",EDGE,"E53")])],"isStart":false})]});}
            var Q1;
            {var subQ0=sQuery(id+"F4.wireOp",EDGE,"E48");var subQ1=sQuery(id+"F4.wireOp",EDGE,"E47");var subQ2=sQuery(id+"F0.wireOp",EDGE,"E12");Q1=makeQuery(id+"F22.opChamfer","BLEND_EDGE",EDGE,{"blendedFrom":[makeQuery(id+"F9.boolean.opBoolean","SPLIT",EDGE,{"disambiguationData":[TD([makeQuery(id+"F1.opExtrude","SWEPT_FACE",FACE,{"disambiguationData":[OSD([subQ2])]})])],"derivedFrom":makeQuery(id+"F5.opExtrude","CAP_EDGE",EDGE,{"disambiguationData":[OSD([subQ0])],"isStart":true})}),makeQuery(id+"F5.opExtrude","CAP_FACE",FACE,{"disambiguationData":[OSD([sQuery(id+"F4.wireOp",EDGE,"E45"),sQuery(id+"F4.wireOp",EDGE,"E46"),subQ1,subQ0,sQuery(id+"F4.wireOp",EDGE,"E49.bottom"),sQuery(id+"F4.wireOp",EDGE,"E49.top"),sQuery(id+"F4.wireOp",EDGE,"E49.left"),sQuery(id+"F4.wireOp",EDGE,"E49.right"),sQuery(id+"F4.wireOp",EDGE,"E50"),sQuery(id+"F4.wireOp",EDGE,"E51"),sQuery(id+"F4.wireOp",EDGE,"E52"),sQuery(id+"F4.wireOp",EDGE,"E53")])],"isStart":false})],"blendedInto":[makeQuery(id+"F5.opExtrude","CAP_FACE",FACE,{"disambiguationData":[OSD([sQuery(id+"F4.wireOp",EDGE,"E45"),sQuery(id+"F4.wireOp",EDGE,"E46"),subQ1,subQ0,sQuery(id+"F4.wireOp",EDGE,"E49.bottom"),sQuery(id+"F4.wireOp",EDGE,"E49.top"),sQuery(id+"F4.wireOp",EDGE,"E49.left"),sQuery(id+"F4.wireOp",EDGE,"E49.right"),sQuery(id+"F4.wireOp",EDGE,"E50"),sQuery(id+"F4.wireOp",EDGE,"E51"),sQuery(id+"F4.wireOp",EDGE,"E52"),sQuery(id+"F4.wireOp",EDGE,"E53")])],"isStart":false})]});}
            var Q2;
            {var subQ0=sQuery(id+"F4.wireOp",EDGE,"E48");var subQ1=sQuery(id+"F4.wireOp",EDGE,"E45");var subQ2=sQuery(id+"F0.wireOp",EDGE,"E10");Q2=makeQuery(id+"F22.opChamfer","BLEND_EDGE",EDGE,{"blendedFrom":[makeQuery(id+"F9.boolean.opBoolean","SPLIT",EDGE,{"disambiguationData":[TD([makeQuery(id+"F1.opExtrude","SWEPT_FACE",FACE,{"disambiguationData":[OSD([subQ2])]})])],"derivedFrom":makeQuery(id+"F5.opExtrude","CAP_EDGE",EDGE,{"disambiguationData":[OSD([subQ0])],"isStart":true})}),makeQuery(id+"F5.opExtrude","CAP_FACE",FACE,{"disambiguationData":[OSD([subQ1,sQuery(id+"F4.wireOp",EDGE,"E46"),sQuery(id+"F4.wireOp",EDGE,"E47"),subQ0,sQuery(id+"F4.wireOp",EDGE,"E49.bottom"),sQuery(id+"F4.wireOp",EDGE,"E49.top"),sQuery(id+"F4.wireOp",EDGE,"E49.left"),sQuery(id+"F4.wireOp",EDGE,"E49.right"),sQuery(id+"F4.wireOp",EDGE,"E50"),sQuery(id+"F4.wireOp",EDGE,"E51"),sQuery(id+"F4.wireOp",EDGE,"E52"),sQuery(id+"F4.wireOp",EDGE,"E53")])],"isStart":false})],"blendedInto":[makeQuery(id+"F5.opExtrude","CAP_FACE",FACE,{"disambiguationData":[OSD([subQ1,sQuery(id+"F4.wireOp",EDGE,"E46"),sQuery(id+"F4.wireOp",EDGE,"E47"),subQ0,sQuery(id+"F4.wireOp",EDGE,"E49.bottom"),sQuery(id+"F4.wireOp",EDGE,"E49.top"),sQuery(id+"F4.wireOp",EDGE,"E49.left"),sQuery(id+"F4.wireOp",EDGE,"E49.right"),sQuery(id+"F4.wireOp",EDGE,"E50"),sQuery(id+"F4.wireOp",EDGE,"E51"),sQuery(id+"F4.wireOp",EDGE,"E52"),sQuery(id+"F4.wireOp",EDGE,"E53")])],"isStart":false})]});}
            fillet(context, id + "F29", {"entities" : qUnion([Q0, Q1, Q2]), "radius" : 1 * mm, "tangentPropagation" : true, "allowEdgeOverflow" : false});
        }
    });
